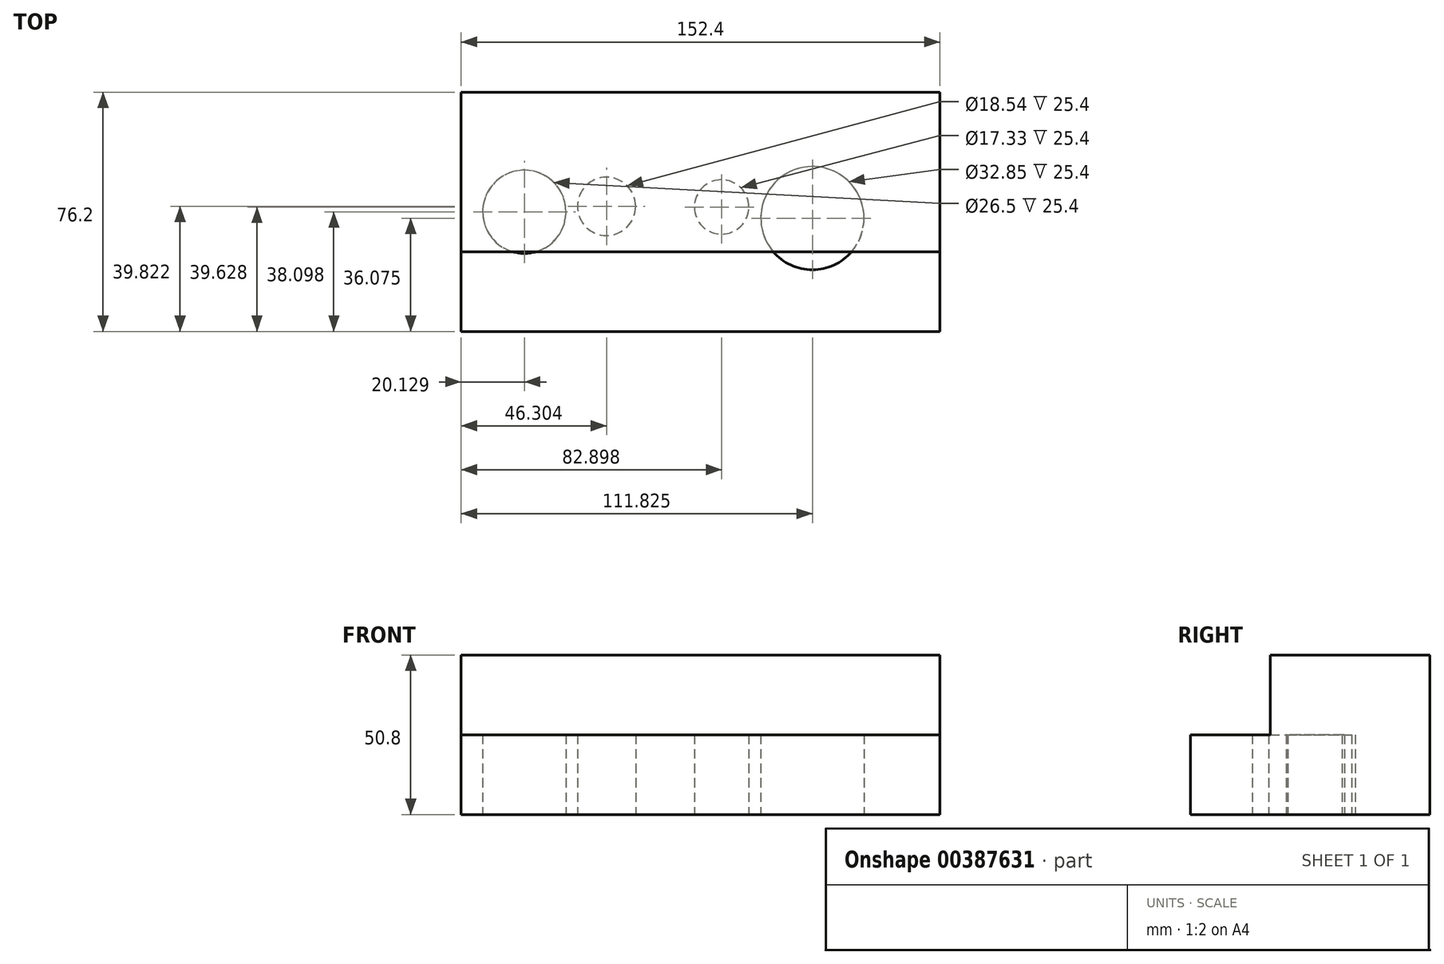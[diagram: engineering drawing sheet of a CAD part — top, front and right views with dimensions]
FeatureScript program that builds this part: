
annotation { "Feature Type Name" : "Feature", "Feature Type Description" : "" }
export const myFeature = defineFeature(function(context is Context, id is Id, definition is map)
    precondition{}
    {
        {
            var Q0;
            Q0=qCreatedBy(makeId("Top.planeOp"),FACE);
            var sketch = newSketch(context, id + "F0", { "sketchPlane" : qUnion([Q0])});
            skLineSegment(sketch, "E0.bottom", {"start": v(-152.4, -81.96) * mm, "end": v(0, -81.96) * mm});
            skLineSegment(sketch, "E0.top", {"start": v(-152.4, -5.76) * mm, "end": v(0, -5.76) * mm});
            skLineSegment(sketch, "E0.left", {"start": v(-152.4, -81.96) * mm, "end": v(-152.4, -5.76) * mm});
            skLineSegment(sketch, "E0.right", {"start": v(0, -81.96) * mm, "end": v(0, -5.76) * mm});
            skCircle(sketch, "E1", {"center": v(-40.58, -45.89) * mm, "radius": 16.42 * mm});
            skCircle(sketch, "E2", {"center": v(-69.5, -42.33) * mm, "radius": 8.67 * mm});
            skCircle(sketch, "E3", {"center": v(-106.1, -42.14) * mm, "radius": 9.27 * mm});
            skCircle(sketch, "E4", {"center": v(-132.27, -43.86) * mm, "radius": 13.25 * mm});
            skPoint(sketch, "E4.centerSnap0", {"position": v(-152.4, -43.86) * mm});
            skSolve(sketch);
        }
        {
            var Q0;
            Q0=qSketchRegion(id+"F0",true);
            extrude(context, id + "F1", {"entities" : qUnion([Q0]), "depth" : 25.4 * mm});
        }
        {
            var Q0;
            Q0=makeQuery(id+"F1.opExtrude","CAP_FACE",FACE,{"disambiguationData":[OSD([sQuery(id+"F0.wireOp",EDGE,"E0.bottom"),sQuery(id+"F0.wireOp",EDGE,"E0.top"),sQuery(id+"F0.wireOp",EDGE,"E0.left"),sQuery(id+"F0.wireOp",EDGE,"E0.right")])],"isStart":false});
            var sketch = newSketch(context, id + "F2", { "sketchPlane" : qUnion([Q0])});
            skLineSegment(sketch, "E5.bottom", {"start": v(-152.4, -5.76) * mm, "end": v(0, -5.76) * mm});
            skLineSegment(sketch, "E5.top", {"start": v(-152.4, -56.56) * mm, "end": v(0, -56.56) * mm});
            skLineSegment(sketch, "E5.left", {"start": v(-152.4, -5.76) * mm, "end": v(-152.4, -56.56) * mm});
            skLineSegment(sketch, "E5.right", {"start": v(0, -5.76) * mm, "end": v(0, -56.56) * mm});
            skSolve(sketch);
        }
        {
            var Q0;
            Q0=qSketchRegion(id+"F2",true);
            extrude(context, id + "F3", {"entities" : qUnion([Q0]), "operationType" : NewBodyOperationType.ADD, "depth" : 25.4 * mm});
        }
    });
